# Revit family: Shower-Bath_and_Handshower_Kit-KOHLER-ELATE-K-28189T_1
name_source: partatom
category: Plumbing Fixtures
revit_build: Autodesk Revit 2017 (Build: 20160225_1515(x64)
units: mm (PartAtom-declared; Revit-internal decimal feet)

## family parameters
Cut with Voids When Loaded = No
Host = Face
OmniClass Number = 23.31.17.00
OmniClass Title = Showers
Part Type = Normal
Room Calculation Point = No
Round Connector Dimension = Use Diameter
Shared = No

## types (2) — shared parameters
ADA Compliant = No
Assembly Code = D2010700
CW Connection = Yes
Cold Water Inlet = Cold Water Inlet
Date Modified = 10/07/2021
Default Elevation = 42"
Description = Wall Mount Bath/Shower Faucet OL
Drain Included = No
Flow Rate = 0 GPM
HW Connection = Yes
Height = 4 15/16"
Hot Water Inlet = Hot Water Inlet
Length = 6 1/8"
Manufacturer = KOHLER Co.
Master Format 2014 = 22 42 23
Master Format 2014 Name = Residential Showers
Material = Premium Metal Construction
Panel Thickness = 4 5/16"
Pressure = 0.00 psi
Product Name = ELATE
URL = http://www.kohler.com.cn
Vent Connection = No
Waste Connection = No
Waste Water Outlet = Waste Water Outlet
WaterSense Certified = No
Width = 5 15/16"

## per-type parameters (varying)
| type | Cover Finish | Finish | Model | Nozzel Finish | Type |
| CP-Polished Chrome | Kohler-Metal-SC-Matte_Chrome | Kohler-Metal-CP-Polished_Chrome | K-28189T-4-CP | Kohler-Plastic-0-White | 1 |
| BL-Matte Black | Kohler-Metal-BL-Matte_Black | Kohler-Metal-BL-Matte_Black | K-28189T-4-BL | Kohler-Plastic-BL-Matte_Black | 2 |

## geometry (parser evidence)
native form markers: Sweep x5
no freeform markers — native parametric forms only
